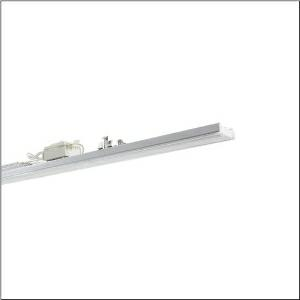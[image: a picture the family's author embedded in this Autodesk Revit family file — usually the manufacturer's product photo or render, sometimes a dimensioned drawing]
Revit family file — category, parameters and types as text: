
# Revit family: licross_11_recessed_mo_51te19dn495g
name_source: partatom
category: Lighting Fixtures
units: mm (PartAtom-declared; Revit-internal decimal feet)

## family parameters
Cut with Voids When Loaded = No
Host = Face
Light Source = No
Part Type = Normal
Room Calculation Point = No
Round Connector Dimension = Use Diameter
Shared = No

## types (1)
- --- (1 x LED, 9810 lm, 56.7 W, 4000K)
    Apparent Load = 57 VA
    CIE Flux Codes = 55 90 98 100 100
    Color Rendering = 80
    Color Temperature = 4000K
    Default Elevation = 1800 mm
    Description = Licross 11 Recessed MO, luminaire insert, of sheet steel, galvanised, coil coated, white, length: 1.500mm, width: 66mm, height: 67mm, LED rated luminous flux: 9.810lm, light colour: 840, SDCM (Standard Deviation of Colour Matching)MacAdam ≤ 2 SDCM (initial), control gear: DALI 2, with plug, 5-pole, with phase selection, mains connection: 220..240V, AC, 50/60Hz, rated input power: 57W, internal wiring halogen-free, primary light control with lens, of plastic, primary optical cover: cover, of PMMA, light emission: direct distribution, primary light characteristic: double asymmetric, protection rating (complete): IP54, insulation class (complete): insulation class I (protective earthing), certification: CE, ENEC, VDE, UKCA, protection symbol: D if used in an environment with non-conductive dust loads with corresponding accessories, impact resistance: IK06, permissible ambient temperature for indoor applications: -25..+35°C, corresponds to IFS (International Featured Standards) requirements for safety and quality in the food industry, reducing of maximum allowable ambient temperature of 5°C with ceiling mounting, LABS conformity tested according to VDMA 24364:2018-05, The light source and the operating device comply with the requirements of the Ecodesign Regulation (EU) 2019/2020 and are replaceable in accordance with this regulation, packaging unit: 1 piece
    Height = 58 mm
    Lamp = 1 x LED
    Lamp Light Flux = 9810 lm
    Lamp Power = 56.7 W
    Lamp count = 1
    Length = 1500 mm
    Luminous efficacy = 173 lm/W
    Manufacturer = Siteco
    ModVariant = No
    Model = 51TE19DN495G
    Mounting Place = Ceiling
    Mounting Type = Pendant
    Number of Poles = 1
    OnlyDefault = Yes
    Power Factor = 1
    Product Name = Licross 11 Recessed MO
    Product group = luminaire insert | ceiling pendant
    ProductGroupID = 901
    Protection Class = Protection class I
    Protection Degree = IP 54
    RLX_Detail_Level = 1
    RLX_Emergency_Light_Flux = 0 lm
    RLX_Emergency_Type = 0
    RLX_Emergency_Type_DB = No
    RlxData = <blob elided: 24797 chars, md5=0805eb79>
    Socket = socket
    Standby Power = 0 W
    System Light Flux = 9810 lm
    System Power = 57 W
    Type Comments = factory setting: luminous flux: 100 % | dim-lin: 254 | 378 mA
    Type Image = l_1296930.jpg
    URL = http://relux.com
    VarID = @adj_102347
    Voltage = 0 V
    Weight = 0.00 kg
    Width = 66 mm

## geometry (parser evidence)
native form markers: Blend x4, Sweep x10
no freeform markers — native parametric forms only
